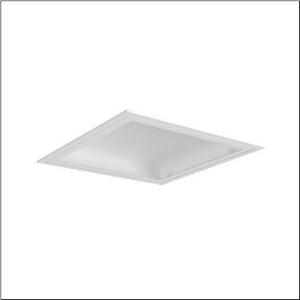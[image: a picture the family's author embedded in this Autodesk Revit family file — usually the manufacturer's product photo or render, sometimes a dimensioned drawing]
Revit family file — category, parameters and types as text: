
# Revit family: mira_r__21_51fr427a462a_66f5
name_source: partatom
category: Lighting Fixtures
units: mm (PartAtom-declared; Revit-internal decimal feet)

## family parameters
Cut with Voids When Loaded = No
Host = Face
Light Source = No
Part Type = Normal
Room Calculation Point = No
Round Connector Dimension = Use Diameter
Shared = No

## types (1)
- Mira® 21 (1 x LED, 6420 lm, 53 W, 4000K)
    Apparent Load = 53 VA
    CIE Flux Codes = 50 81 97 100 100
    Color Rendering = 80
    Color Temperature = 4000K
    Default Elevation = 1800 mm
    Description = Mira® 21, clean room luminaire, primary light control with reflector, primary optical cover: cover, of PC, light emission: direct distribution, primary light characteristic: symmetric, installation type: recessed, LED, rated luminous flux: 6.420lm, luminous efficacy: 121lm/W, light colour: 840, colour temperature: 4000K, control gear: ON/OFF, with terminal, 3-pole, max. 2.5mm², mains connection: 230V, AC, 50/60Hz, rated input power: 53W, luminaire housing, of sheet steel, coated, pure white (RAL 9010), with concealed spring brackets, module: M625, length: 623mm, width: 623mm, height: 115mm, protection rating (complete): IP54, insulation class (complete): insulation class I (protective earthing), certification: CE, UKCA, permissible operating ambient temperature: -5..+40°C, standard: EN 50419, packaging unit: 1 piece
    Height = 0 mm  [stored 0 ft]
    Lamp = 1 x LED
    Lamp Light Flux = 6420 lm
    Lamp Power = 53 W
    Lamp count = 1
    Length = 625 mm
    Luminous efficacy = 121 lm/W
    Manufacturer = Siteco
    ModVariant = No
    Model = 51FR427A462A
    Mounting Place = Ceiling
    Mounting Type = Recessed
    Number of Poles = 1
    OnlyDefault = Yes
    Power Factor = 1
    Product Name = Mira® 21
    Product group = clean room luminaire | ceiling recessed
    ProductGroupID = 402
    Protection Class = Protection class I
    Protection Degree = IP 54
    RLX_Detail_Level = 1
    RLX_Emergency_Light_Flux = 0 lm
    RLX_Emergency_Type = 0
    RLX_Emergency_Type_DB = No
    RlxData = <blob elided: 13413 chars, md5=5e3a4e81>
    Socket = socket
    Standby Power = 0 W
    System Light Flux = 6420 lm
    System Power = 53 W
    Type Comments = Product without accessories
    Type Image = l_1007109.jpg
    URL = http://relux.com
    VarID = ---
    Voltage = 0 V
    Weight = 0.00 kg
    Width = 625 mm

note: [stored X ft] marks values corroborated as IEEE doubles in the binary element streams (Revit-internal decimal feet)

## geometry (parser evidence)
native form markers: Sweep x9
no freeform markers — native parametric forms only
